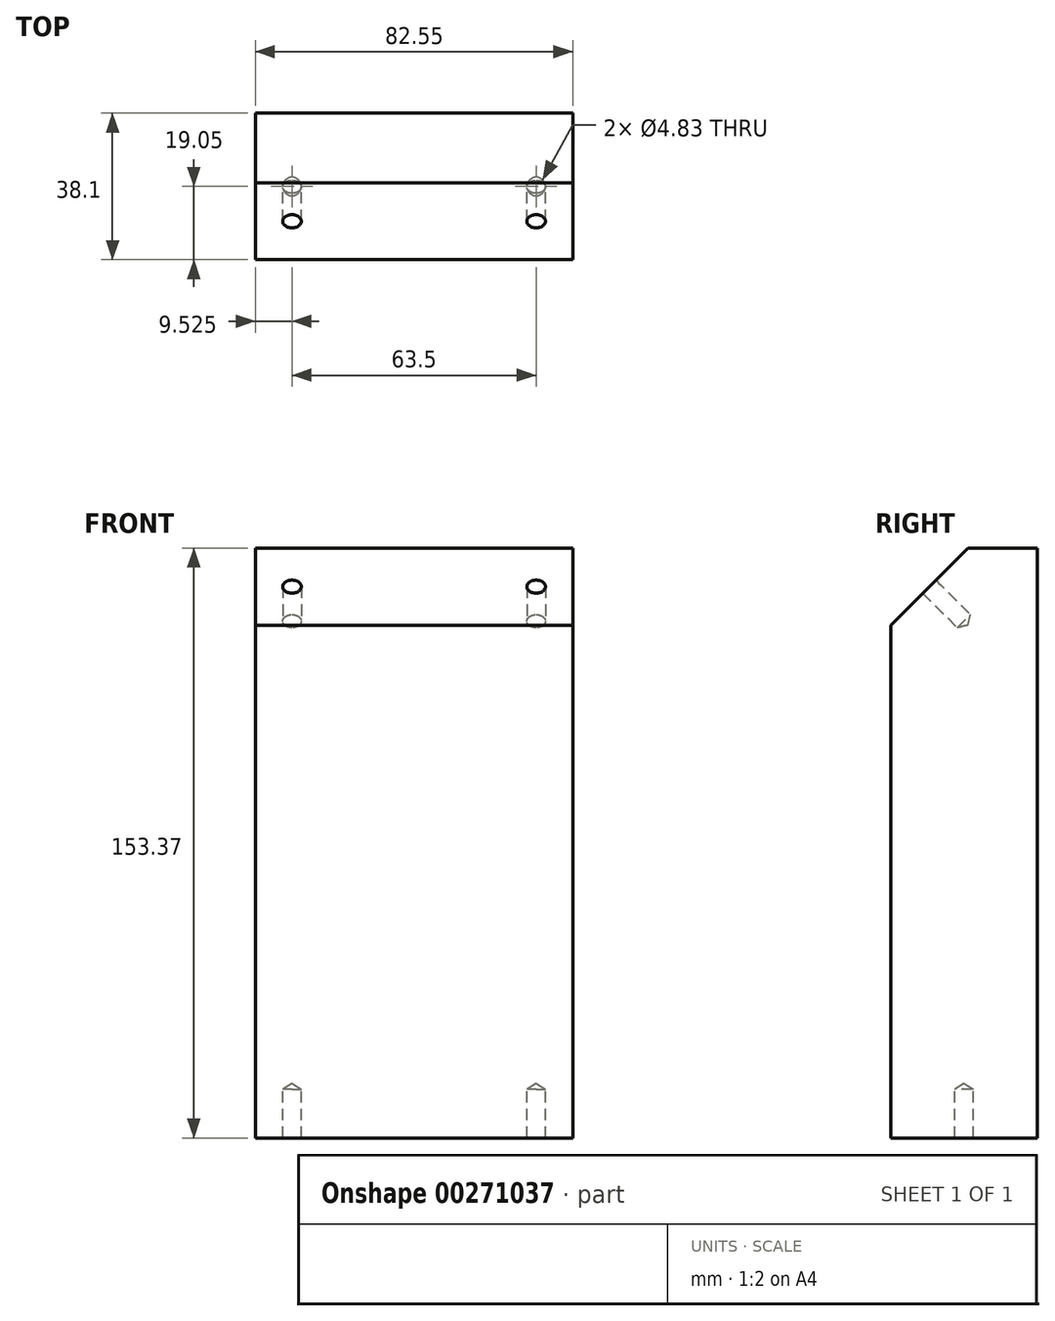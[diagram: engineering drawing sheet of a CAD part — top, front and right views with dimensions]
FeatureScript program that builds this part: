
annotation { "Feature Type Name" : "Feature", "Feature Type Description" : "" }
export const myFeature = defineFeature(function(context is Context, id is Id, definition is map)
    precondition{}
    {
        {
            var Q0;
            Q0=qCreatedBy(makeId("Front.planeOp"),FACE);
            var sketch = newSketch(context, id + "F0", { "sketchPlane" : qUnion([Q0])});
            skLineSegment(sketch, "E0.bottom", {"start": v(0, 0) * mm, "end": v(82.55, 0) * mm});
            skLineSegment(sketch, "E0.top", {"start": v(0, 153.37) * mm, "end": v(82.55, 153.37) * mm});
            skLineSegment(sketch, "E0.left", {"start": v(0, 0) * mm, "end": v(0, 153.37) * mm});
            skLineSegment(sketch, "E0.right", {"start": v(82.55, 0) * mm, "end": v(82.55, 153.37) * mm});
            skSolve(sketch);
        }
        {
            var Q0;
            Q0 = qSketchRegion(id + "F0", true);
            extrude(context, id + "F1", {"entities" : qUnion([Q0]), "depth" : 38.1 * mm});
        }
        {
            var Q0;
            Q0=makeQuery(id+"F1.opExtrude","CAP_EDGE",EDGE,{"disambiguationData":[OSD([sQuery(id+"F0.wireOp",EDGE,"E0.top")])],"isStart":false});
            chamfer(context, id + "F2", {"entities" : qUnion([Q0]), "chamferType" : ChamferType.OFFSET_ANGLE, "width" : 20.02 * mm, "oppositeDirection" : false, "angle" : 45 * degree, "tangentPropagation" : true});
        }
        {
            var Q0;
            Q0=makeQuery(id+"F2.opChamfer","BLEND_FACE",FACE,{"disambiguationData":[OSD([sQuery(id+"F0.wireOp",EDGE,"E0.top")])]});
            var sketch = newSketch(context, id + "F3", { "sketchPlane" : qUnion([Q0])});
            skPoint(sketch, "E1", {"position": v(9.53, 81.5) * mm});
            skPoint(sketch, "E1.positionSnap0", {"position": v(0, 81.5) * mm});
            skPoint(sketch, "E2", {"position": v(73.03, 81.5) * mm});
            skSolve(sketch);
        }
        {
            var Q0;
            Q0=makeQuery(id+"F1.opExtrude","SWEPT_FACE",FACE,{"disambiguationData":[OSD([sQuery(id+"F0.wireOp",EDGE,"E0.bottom")])]});
            var sketch = newSketch(context, id + "F4", { "sketchPlane" : qUnion([Q0])});
            skPoint(sketch, "E3", {"position": v(9.52, 19.05) * mm});
            skPoint(sketch, "E3.positionSnap0", {"position": v(0, 19.05) * mm});
            skPoint(sketch, "E4", {"position": v(73.03, 19.05) * mm});
            skSolve(sketch);
        }
        {
            var Q0;
            Q0=sQuery(id+"F3.wireOp",VERTEX,"E1");
            var Q1;
            Q1=sQuery(id+"F3.wireOp",VERTEX,"E2");
            var Q2;
            Q2=sQuery(id+"F4.wireOp",VERTEX,"E3");
            var Q3;
            Q3=sQuery(id+"F4.wireOp",VERTEX,"E4");
            var Q4;
            Q4=makeQuery(id+"F1.opExtrude","SWEPT_BODY",BODY,{"disambiguationData":[OSD([sQuery(id+"F0.wireOp",EDGE,"E0.bottom"),sQuery(id+"F0.wireOp",EDGE,"E0.top"),sQuery(id+"F0.wireOp",EDGE,"E0.left"),sQuery(id+"F0.wireOp",EDGE,"E0.right")])]});
            hole(context, id + "F5", {"style" : HoleStyle.SIMPLE, "endStyle" : HoleEndStyle.BLIND, "holeDiameter" : 4.83 * mm, "holeDepth" : 12.7 * mm, "tappedDepth" : 12.7 * mm, "tapClearance" : 3, "locations" : qUnion([Q0, Q1, Q2, Q3]), "scope" : qUnion([Q4])});
        }
    });
